# Revit family: Diverter_Trim-Grohe-Concetto-29104_Series
name_source: partatom
category: Plumbing Fixtures
units: mm (PartAtom-declared; Revit-internal decimal feet)

## family parameters
Cut with Voids When Loaded = No
Host = Face
OmniClass Number = 23.45.05.14.17
OmniClass Title = Showers
Part Type = Normal
Room Calculation Point = No
Round Connector Dimension = Use Diameter
Shared = Yes

## types (2) — shared parameters
ADA Compliant = Yes
Assembly Code = D2020
CW Connection = Yes
CWFU = 3
Default Elevation = 0"
Description = Concetto 2-Way Diverter Trim (Shower head/Tub Spout)
HW Connection = Yes
HWFU = 3
Height = 4 13/16"
IAPMO Compliance = cUPC
Installation Type = Surface Mounted
Length = 2 5/8"
Manufacturer = GROHE
Price = Prices may vary. Please consult Manufacturer Representative for most up-to-date price list.
Product Documentation Link = https://americanstandard.box.com
Product Page URL = https://www.grohe.us
Revised Date = 6/28/2021
Tempered Water Connection Diameter = 1/2"
Tempered Water Connection Radius = 1/4"
URL = http://www.grohe.com
Vent Connection = No
WFU = 4
Warranty Information = Limited Lifetime Warranty
Waste Connection = No
Width = 3 1/8"

## per-type parameters (varying)
| type | Finish | Material |
| 29104001 | Metal-Grohe-001-Chrome | Metal-Grohe-001-Chrome |
| 29104EN1 | Metal-Grohe-EN1-Brushed Nickel | Metal-Grohe-EN1-Brushed Nickel |

note: column(s) folded — value = type name in every type: Model

## geometry (parser evidence)
native form markers: Sweep x3
no freeform markers — native parametric forms only
